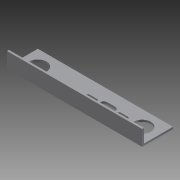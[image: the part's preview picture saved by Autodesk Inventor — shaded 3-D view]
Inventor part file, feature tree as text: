
AUTODESK INVENTOR PART (.ipt)
format: ipt  version: 2012 (Build 160160000, 160)  size: 106,496 bytes
history: native  units: in
note: dims shown in document units (in); Inventor stores cm internally (conversion verified against a paired STEP export)
features: other x3, sketch x2, extrude x1
ambient origin geometry x8: Origin, YZ Plane, XZ Plane, XY Plane, X Axis, Y Axis, Z Axis, Center Point
bodies: Solid1 (feature_tree)
feature tree (6):
  other  "8 ball bottom 1 by 2 L short.ipt"
  extrude  "Extrusion1"  Depth=0.1in
  other  "Solid1::8 ball bottom 1 by 2 L short.ipt"
  sketch  "Sketch1"  dims[d0=0.3937in d1=0.1in]
  sketch  "Sketch2"  dims[d2=0.5in d3=0.25in d4=0.5in d5=1.0in d6=1.0in d7=0.7874in d9=2.0in d10=0.3937in d12=1.0in d14=1.0in d15=0.0in]
  other  "TaggingFeature1"
